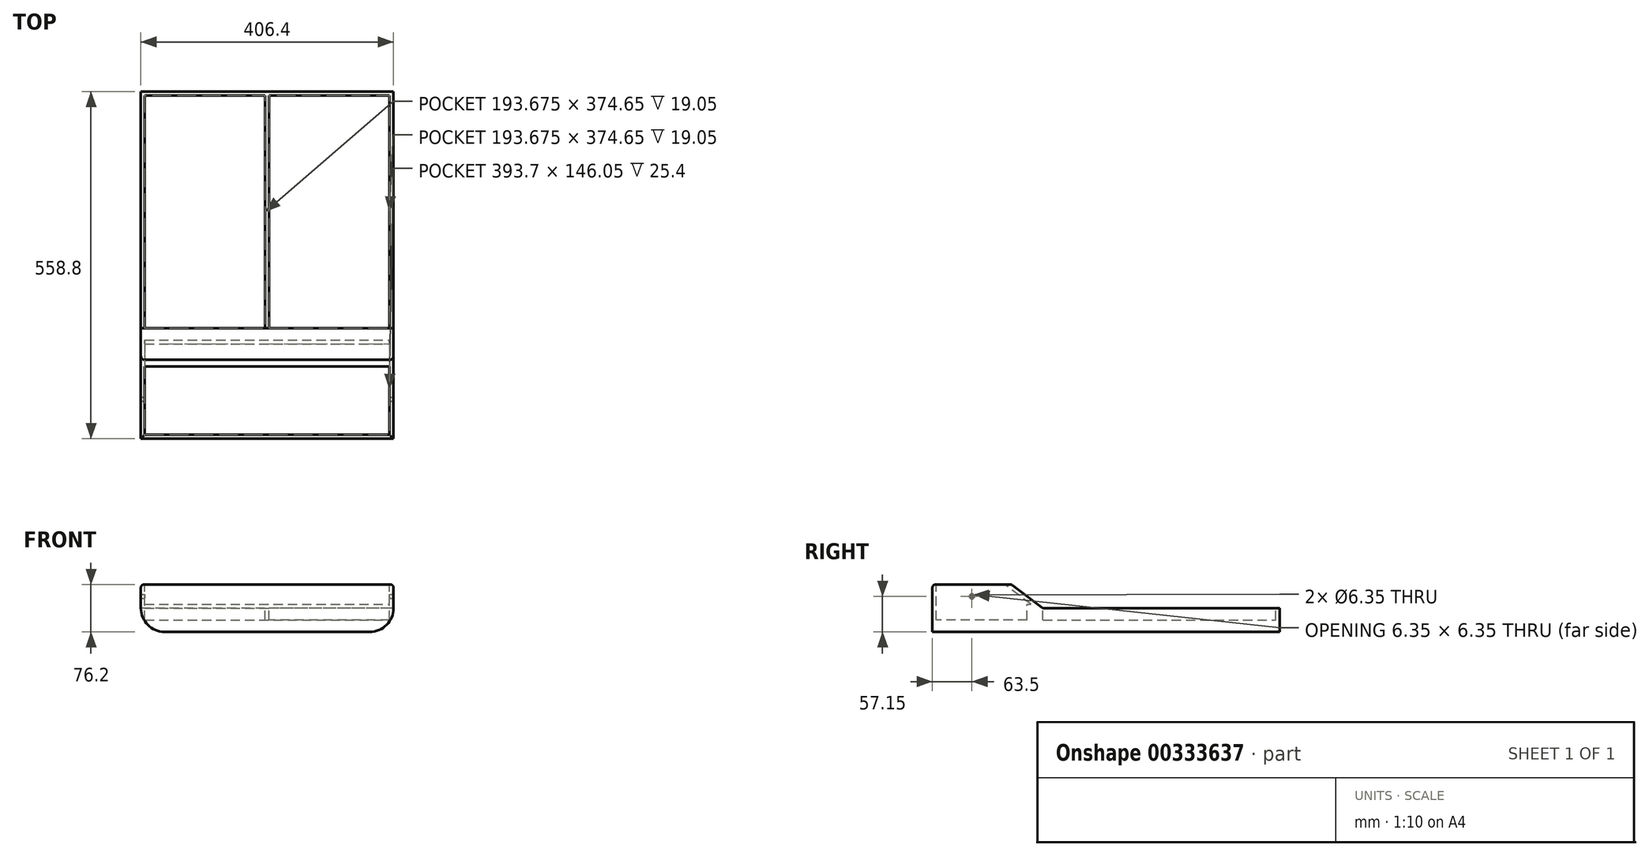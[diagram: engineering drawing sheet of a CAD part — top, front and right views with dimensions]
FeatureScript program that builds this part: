
annotation { "Feature Type Name" : "Feature", "Feature Type Description" : "" }
export const myFeature = defineFeature(function(context is Context, id is Id, definition is map)
    precondition{}
    {
        {
            var Q0;
            Q0=qCreatedBy(makeId("Top.planeOp"),FACE);
            var sketch = newSketch(context, id + "F0", { "sketchPlane" : qUnion([Q0])});
            skLineSegment(sketch, "E0.bottom", {"start": v(-463.02, 274.37) * mm, "end": v(-56.62, 274.37) * mm});
            skLineSegment(sketch, "E0.top", {"start": v(-463.02, -284.43) * mm, "end": v(-56.62, -284.43) * mm});
            skLineSegment(sketch, "E0.left", {"start": v(-463.02, 274.37) * mm, "end": v(-463.02, -284.43) * mm});
            skLineSegment(sketch, "E0.right", {"start": v(-56.62, 274.37) * mm, "end": v(-56.62, -284.43) * mm});
            skPoint(sketch, "E0.middle", {"position": v(-259.82, -5.03) * mm});
            skSolve(sketch);
        }
        {
            var Q0;
            Q0 = qSketchRegion(id + "F0", true);
            var Q1;
            Q1=makeQuery(id+"F0.imprint","IMPRINT",FACE,{"disambiguationData":[TD([[makeQuery(id+"F0.imprint","IMPRINT",EDGE,{"derivedFrom":sQuery(id+"F0.wireOp",EDGE,"E0.bottom")}),-1.0]])]});
            extrude(context, id + "F1", {"entities" : qUnion([Q0, Q1]), "depth" : 76.2 * mm});
        }
        {
            var Q0;
            Q0=makeQuery(id+"F1.opExtrude","SWEPT_FACE",FACE,{"disambiguationData":[OSD([sQuery(id+"F0.wireOp",EDGE,"E0.left")])]});
            var sketch = newSketch(context, id + "F2", { "sketchPlane" : qUnion([Q0])});
            skLineSegment(sketch, "E1", {"start": v(-274.37, 76.2) * mm, "end": v(-147.37, 76.2) * mm});
            skLineSegment(sketch, "E2", {"start": v(5.03, 76.2) * mm, "end": v(5.03, 0) * mm});
            skLineSegment(sketch, "E3.MirrorCS", {"start": v(284.43, 76.2) * mm, "end": v(157.43, 76.2) * mm});
            skLineSegment(sketch, "E4", {"start": v(5.03, 38.1) * mm, "end": v(-96.57, 38.1) * mm});
            skPoint(sketch, "E4.endSnap0", {"position": v(5.03, 38.1) * mm});
            skLineSegment(sketch, "E5.MirrorCS", {"start": v(5.03, 38.1) * mm, "end": v(106.63, 38.1) * mm});
            skLineSegment(sketch, "E6", {"start": v(-147.37, 76.2) * mm, "end": v(-96.57, 38.1) * mm});
            skLineSegment(sketch, "E7", {"start": v(106.63, 38.1) * mm, "end": v(157.43, 76.2) * mm});
            skLineSegment(sketch, "E8", {"start": v(-147.37, 76.2) * mm, "end": v(157.43, 76.2) * mm});
            skLineSegment(sketch, "E9", {"start": v(-96.57, 38.1) * mm, "end": v(-274.37, 38.1) * mm});
            skLineSegment(sketch, "E10", {"start": v(-274.37, 38.1) * mm, "end": v(-274.37, 76.2) * mm});
            skSolve(sketch);
        }
        {
            var Q0;
            {var subQ3=sQuery(id+"F2.wireOp",EDGE,"E4");Q0=makeQuery(id+"F2.imprint","IMPRINT",FACE,{"disambiguationData":[TD([[makeQuery(id+"F2.imprint","IMPRINT",EDGE,{"derivedFrom":subQ3}),-1.0]])]});}
            var Q1;
            {var subQ3=sQuery(id+"F2.wireOp",EDGE,"E5.MirrorCS");Q1=makeQuery(id+"F2.imprint","IMPRINT",FACE,{"disambiguationData":[TD([[makeQuery(id+"F2.imprint","IMPRINT",EDGE,{"derivedFrom":subQ3}),1.0]])]});}
            var Q2;
            Q2=makeQuery(id+"F2.imprint","IMPRINT",FACE,{"disambiguationData":[TD([[makeQuery(id+"F2.imprint","IMPRINT",EDGE,{"derivedFrom":sQuery(id+"F2.wireOp",EDGE,"E1")}),-1.0]])]});
            extrude(context, id + "F3", {"entities" : qUnion([Q0, Q1, Q2]), "operationType" : NewBodyOperationType.REMOVE, "oppositeDirection" : true, "depth" : 406.4 * mm});
        }
        {
            var Q0;
            Q0=makeQuery(id+"F1.opExtrude","CAP_EDGE",EDGE,{"disambiguationData":[OSD([sQuery(id+"F0.wireOp",EDGE,"E0.right")])],"isStart":true});
            var Q1;
            Q1=makeQuery(id+"F1.opExtrude","CAP_EDGE",EDGE,{"disambiguationData":[OSD([sQuery(id+"F0.wireOp",EDGE,"E0.left")])],"isStart":true});
            fillet(context, id + "F4", {"entities" : qUnion([Q0, Q1]), "radius" : 38.1 * mm, "tangentPropagation" : true, "allowEdgeOverflow" : false});
        }
        {
            var Q0;
            Q0=makeQuery(id+"F3.boolean.opBoolean","COPY",FACE,{"derivedFrom":makeQuery(id+"F3.opExtrude","SWEPT_FACE",FACE,{"disambiguationData":[OSD([sQuery(id+"F2.wireOp",EDGE,"E4"),sQuery(id+"F2.wireOp",EDGE,"E5.MirrorCS"),sQuery(id+"F2.wireOp",EDGE,"E9")])]})});
            var sketch = newSketch(context, id + "F5", { "sketchPlane" : qUnion([Q0])});
            skLineSegment(sketch, "E11.bottom", {"start": v(-456.67, 268.02) * mm, "end": v(-62.97, 268.02) * mm});
            skLineSegment(sketch, "E11.top", {"start": v(-456.67, -106.63) * mm, "end": v(-62.97, -106.63) * mm});
            skLineSegment(sketch, "E11.left", {"start": v(-456.67, 268.02) * mm, "end": v(-456.67, -106.63) * mm});
            skLineSegment(sketch, "E11.right", {"start": v(-62.97, 268.02) * mm, "end": v(-62.97, -106.63) * mm});
            skSolve(sketch);
        }
        {
            var Q0;
            Q0=makeQuery(id+"F5.imprint","IMPRINT",FACE,{"disambiguationData":[TD([[makeQuery(id+"F5.imprint","IMPRINT",EDGE,{"derivedFrom":sQuery(id+"F5.wireOp",EDGE,"E11.bottom")}),-1.0]])]});
            extrude(context, id + "F6", {"entities" : qUnion([Q0]), "operationType" : NewBodyOperationType.REMOVE, "oppositeDirection" : true, "depth" : 19.05 * mm});
        }
        {
            var Q0;
            Q0=makeQuery(id+"F1.opExtrude","SWEPT_FACE",FACE,{"disambiguationData":[OSD([sQuery(id+"F0.wireOp",EDGE,"E0.right")])]});
            var sketch = newSketch(context, id + "F7", { "sketchPlane" : qUnion([Q0])});
            skLineSegment(sketch, "E12", {"start": v(-278.08, 44.45) * mm, "end": v(-125.68, 44.45) * mm});
            skLineSegment(sketch, "E13", {"start": v(-125.68, 44.45) * mm, "end": v(-168.01, 76.2) * mm});
            skLineSegment(sketch, "E14", {"start": v(-168.01, 76.2) * mm, "end": v(-278.08, 76.2) * mm});
            skLineSegment(sketch, "E15", {"start": v(-278.08, 44.45) * mm, "end": v(-278.08, 76.2) * mm});
            skSolve(sketch);
        }
        {
            var Q0;
            Q0=makeQuery(id+"F7.imprint","IMPRINT",FACE,{"disambiguationData":[TD([[makeQuery(id+"F7.imprint","IMPRINT",EDGE,{"derivedFrom":sQuery(id+"F7.wireOp",EDGE,"E12")}),1.0]])]});
            extrude(context, id + "F8", {"entities" : qUnion([Q0]), "operationType" : NewBodyOperationType.REMOVE, "oppositeDirection" : true, "depth" : 406.4 * mm, "hasSecondDirection" : true, "secondDirectionOppositeDirection" : false, "secondDirectionDepth" : 6.35 * mm});
        }
        {
            var Q0;
            Q0=makeQuery(id+"F8.boolean.opBoolean","COPY",FACE,{"derivedFrom":makeQuery(id+"F8.opExtrude","SWEPT_FACE",FACE,{"disambiguationData":[OSD([sQuery(id+"F7.wireOp",EDGE,"E12")])]})});
            var sketch = newSketch(context, id + "F9", { "sketchPlane" : qUnion([Q0])});
            skLineSegment(sketch, "E16.bottom", {"start": v(-456.67, -132.03) * mm, "end": v(-62.97, -132.03) * mm});
            skLineSegment(sketch, "E16.top", {"start": v(-456.67, -278.08) * mm, "end": v(-62.97, -278.08) * mm});
            skLineSegment(sketch, "E16.left", {"start": v(-456.67, -132.03) * mm, "end": v(-456.67, -278.08) * mm});
            skLineSegment(sketch, "E16.right", {"start": v(-62.97, -132.03) * mm, "end": v(-62.97, -278.08) * mm});
            skSolve(sketch);
        }
        {
            var Q0;
            Q0=makeQuery(id+"F9.imprint","IMPRINT",FACE,{"disambiguationData":[TD([[makeQuery(id+"F9.imprint","IMPRINT",EDGE,{"derivedFrom":sQuery(id+"F9.wireOp",EDGE,"E16.bottom")}),-1.0]])]});
            extrude(context, id + "F10", {"entities" : qUnion([Q0]), "operationType" : NewBodyOperationType.REMOVE, "oppositeDirection" : true, "depth" : 25.4 * mm});
        }
        {
            var Q0;
            Q0=makeQuery(id+"F1.opExtrude","SWEPT_FACE",FACE,{"disambiguationData":[OSD([sQuery(id+"F0.wireOp",EDGE,"E0.right")])]});
            var sketch = newSketch(context, id + "F11", { "sketchPlane" : qUnion([Q0])});
            skLineSegment(sketch, "E17", {"start": v(-278.08, 76.2) * mm, "end": v(-168.01, 76.2) * mm});
            skLineSegment(sketch, "E18", {"start": v(-168.01, 76.2) * mm, "end": v(-125.68, 44.45) * mm});
            skLineSegment(sketch, "E19", {"start": v(-125.68, 44.45) * mm, "end": v(-278.08, 44.45) * mm});
            skLineSegment(sketch, "E20", {"start": v(-278.08, 44.45) * mm, "end": v(-278.08, 76.2) * mm});
            skSolve(sketch);
        }
        {
            var Q0;
            Q0=makeQuery(id+"F11.imprint","IMPRINT",FACE,{"disambiguationData":[TD([[makeQuery(id+"F11.imprint","IMPRINT",EDGE,{"derivedFrom":sQuery(id+"F11.wireOp",EDGE,"E17")}),-1.0]])]});
            extrude(context, id + "F12", {"entities" : qUnion([Q0]), "operationType" : NewBodyOperationType.ADD, "oppositeDirection" : true, "depth" : 6.35 * mm});
        }
        {
            var Q0;
            Q0=makeQuery(id+"F1.opExtrude","SWEPT_FACE",FACE,{"disambiguationData":[OSD([sQuery(id+"F0.wireOp",EDGE,"E0.left")])]});
            var sketch = newSketch(context, id + "F13", { "sketchPlane" : qUnion([Q0])});
            skLineSegment(sketch, "E21", {"start": v(125.68, 44.45) * mm, "end": v(168.01, 76.2) * mm});
            skLineSegment(sketch, "E22", {"start": v(168.01, 76.2) * mm, "end": v(278.08, 76.2) * mm});
            skLineSegment(sketch, "E23", {"start": v(278.08, 76.2) * mm, "end": v(278.08, 44.45) * mm});
            skLineSegment(sketch, "E24", {"start": v(278.08, 44.45) * mm, "end": v(125.68, 44.45) * mm});
            skSolve(sketch);
        }
        {
            var Q0;
            Q0=makeQuery(id+"F13.imprint","IMPRINT",FACE,{"disambiguationData":[TD([[makeQuery(id+"F13.imprint","IMPRINT",EDGE,{"derivedFrom":sQuery(id+"F13.wireOp",EDGE,"E21")}),-1.0]])]});
            extrude(context, id + "F14", {"entities" : qUnion([Q0]), "operationType" : NewBodyOperationType.ADD, "oppositeDirection" : true, "depth" : 6.35 * mm});
        }
        {
            var Q0;
            Q0=makeQuery(id+"F12.boolean.opBoolean","MERGE",FACE,{"derivedFrom":[makeQuery(id+"F1.opExtrude","SWEPT_FACE",FACE,{"disambiguationData":[OSD([sQuery(id+"F0.wireOp",EDGE,"E0.right")])]}),makeQuery(id+"F12.opExtrude","CAP_FACE",FACE,{"disambiguationData":[OSD([sQuery(id+"F11.wireOp",EDGE,"E17"),sQuery(id+"F11.wireOp",EDGE,"E18"),sQuery(id+"F11.wireOp",EDGE,"E19"),sQuery(id+"F11.wireOp",EDGE,"E20")])],"isStart":true})]});
            var sketch = newSketch(context, id + "F15", { "sketchPlane" : qUnion([Q0])});
            skCircle(sketch, "E25", {"center": v(-220.93, 57.15) * mm, "radius": 3.18 * mm});
            skSolve(sketch);
        }
        {
            var Q0;
            Q0=makeQuery(id+"F15.imprint","IMPRINT",FACE,{"disambiguationData":[TD([[makeQuery(id+"F15.imprint","IMPRINT",EDGE,{"derivedFrom":sQuery(id+"F15.wireOp",EDGE,"E25")}),1.0]])]});
            extrude(context, id + "F16", {"entities" : qUnion([Q0]), "operationType" : NewBodyOperationType.REMOVE, "endBound" : BoundingType.THROUGH_ALL, "oppositeDirection" : true, "depth" : 25.4 * mm});
        }
        {
            var Q0;
            {var subQ0=sQuery(id+"F0.wireOp",EDGE,"E0.left");var subQ1=sQuery(id+"F0.wireOp",EDGE,"E0.top");var subQ4=makeQuery(id+"F1.opExtrude","CAP_EDGE",EDGE,{"disambiguationData":[OSD([subQ0])],"isStart":false});Q0=makeQuery(id+"F14.boolean.opBoolean","MERGE",EDGE,{"derivedFrom":[makeQuery(id+"F8.boolean.opBoolean","SPLIT",EDGE,{"disambiguationData":[TD([makeQuery(id+"F1.opExtrude","SWEPT_FACE",FACE,{"disambiguationData":[OSD([subQ1])]})])],"derivedFrom":subQ4}),makeQuery(id+"F8.boolean.opBoolean","SPLIT",EDGE,{"disambiguationData":[TD([makeQuery(id+"F3.boolean.opBoolean","COPY",FACE,{"derivedFrom":makeQuery(id+"F3.opExtrude","SWEPT_FACE",FACE,{"disambiguationData":[OSD([sQuery(id+"F2.wireOp",EDGE,"E7")])]})})])],"derivedFrom":subQ4}),makeQuery(id+"F14.opExtrude","CAP_EDGE",EDGE,{"disambiguationData":[OSD([sQuery(id+"F13.wireOp",EDGE,"E22")])],"isStart":true})]});}
            var Q1;
            Q1=makeQuery(id+"F3.boolean.opBoolean","COPY",EDGE,{"derivedFrom":makeQuery(id+"F3.opExtrude","SWEPT_EDGE",EDGE,{"disambiguationData":[OSD([sQuery(id+"F2.wireOp",EDGE,"E3.MirrorCS"),sQuery(id+"F2.wireOp",EDGE,"E7"),sQuery(id+"F2.wireOp",EDGE,"E8")])]})});
            var Q2;
            Q2=makeQuery(id+"F1.opExtrude","CAP_EDGE",EDGE,{"disambiguationData":[OSD([sQuery(id+"F0.wireOp",EDGE,"E0.top")])],"isStart":false});
            var Q3;
            {var subQ0=sQuery(id+"F0.wireOp",EDGE,"E0.right");var subQ1=sQuery(id+"F0.wireOp",EDGE,"E0.top");var subQ4=makeQuery(id+"F1.opExtrude","CAP_EDGE",EDGE,{"disambiguationData":[OSD([subQ0])],"isStart":false});Q3=makeQuery(id+"F12.boolean.opBoolean","MERGE",EDGE,{"derivedFrom":[makeQuery(id+"F8.boolean.opBoolean","SPLIT",EDGE,{"disambiguationData":[TD([makeQuery(id+"F1.opExtrude","SWEPT_FACE",FACE,{"disambiguationData":[OSD([subQ1])]})])],"derivedFrom":subQ4}),makeQuery(id+"F8.boolean.opBoolean","SPLIT",EDGE,{"disambiguationData":[TD([makeQuery(id+"F3.boolean.opBoolean","COPY",FACE,{"derivedFrom":makeQuery(id+"F3.opExtrude","SWEPT_FACE",FACE,{"disambiguationData":[OSD([sQuery(id+"F2.wireOp",EDGE,"E7")])]})})])],"derivedFrom":subQ4}),makeQuery(id+"F12.opExtrude","CAP_EDGE",EDGE,{"disambiguationData":[OSD([sQuery(id+"F11.wireOp",EDGE,"E17")])],"isStart":true})]});}
            fillet(context, id + "F17", {"entities" : qUnion([Q0, Q1, Q2, Q3]), "radius" : 5.08 * mm, "tangentPropagation" : true, "allowEdgeOverflow" : false});
        }
        {
            var Q0;
            Q0=makeQuery(id+"F1.opExtrude","SWEPT_FACE",FACE,{"disambiguationData":[OSD([sQuery(id+"F0.wireOp",EDGE,"E0.bottom")])]});
            var sketch = newSketch(context, id + "F18", { "sketchPlane" : qUnion([Q0])});
            skLineSegment(sketch, "E26.bottom", {"start": v(263, 38.1) * mm, "end": v(256.65, 38.1) * mm});
            skLineSegment(sketch, "E26.top", {"start": v(263, 0) * mm, "end": v(256.65, 0) * mm});
            skLineSegment(sketch, "E26.left", {"start": v(263, 38.1) * mm, "end": v(263, 0) * mm});
            skLineSegment(sketch, "E26.right", {"start": v(256.65, 38.1) * mm, "end": v(256.65, 0) * mm});
            skPoint(sketch, "E26.middle", {"position": v(259.82, 19.05) * mm});
            skSolve(sketch);
        }
        {
            var Q0;
            Q0 = qSketchRegion(id + "F18", true);
            var Q1;
            Q1=makeQuery(id+"F6.boolean.opBoolean","COPY",FACE,{"derivedFrom":makeQuery(id+"F6.opExtrude","SWEPT_FACE",FACE,{"disambiguationData":[OSD([sQuery(id+"F5.wireOp",EDGE,"E11.top")])]})});
            extrude(context, id + "F19", {"entities" : qUnion([Q0]), "operationType" : NewBodyOperationType.ADD, "endBound" : BoundingType.UP_TO_SURFACE, "oppositeDirection" : true, "endBoundEntityFace" : qUnion([Q1]), "depth" : 25.4 * mm});
        }
    });
